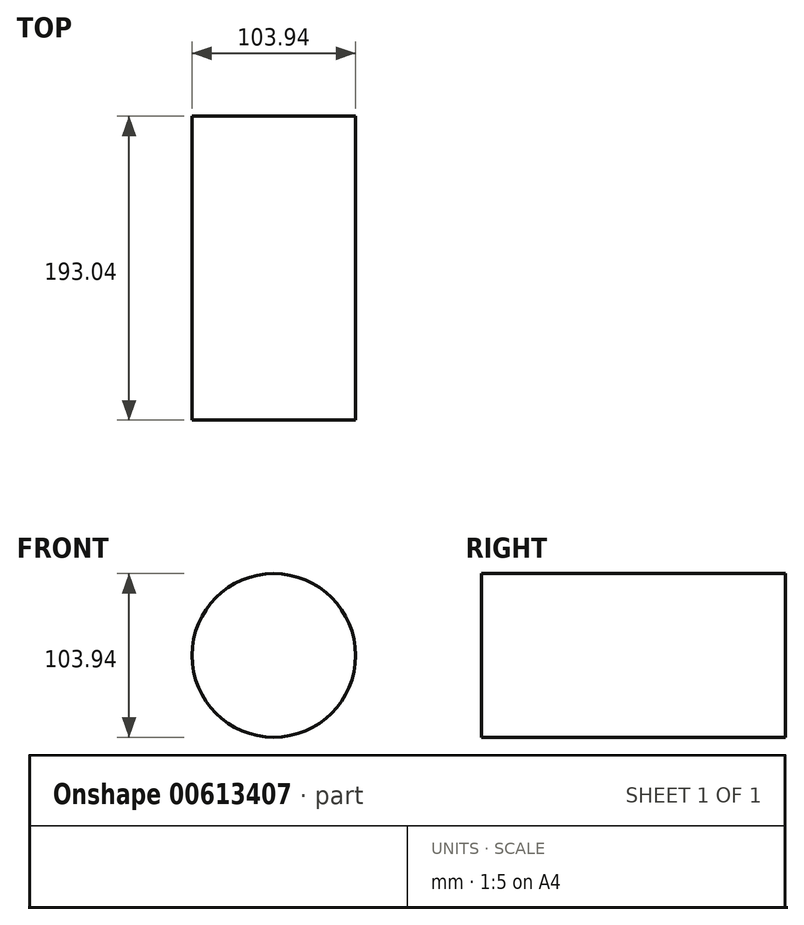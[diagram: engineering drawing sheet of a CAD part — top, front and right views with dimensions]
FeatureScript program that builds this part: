
annotation { "Feature Type Name" : "Feature", "Feature Type Description" : "" }
export const myFeature = defineFeature(function(context is Context, id is Id, definition is map)
    precondition{}
    {
        {
            var Q0;
            Q0=qCreatedBy(makeId("Front.planeOp"),FACE);
            var sketch = newSketch(context, id + "F0", { "sketchPlane" : qUnion([Q0])});
            skCircle(sketch, "E0", {"center": v(-63.15, 31.99) * mm, "radius": 51.97 * mm});
            skSolve(sketch);
        }
        {
            var Q0;
            Q0=makeQuery(id+"F0.imprint","IMPRINT",FACE,{"disambiguationData":[TD([[makeQuery(id+"F0.imprint","IMPRINT",EDGE,{"derivedFrom":sQuery(id+"F0.wireOp",EDGE,"E0")}),1.0]])]});
            extrude(context, id + "F1", {"entities" : qUnion([Q0]), "depth" : 193.04 * mm, "offsetDistance" : 25.4 * mm});
        }
    });
